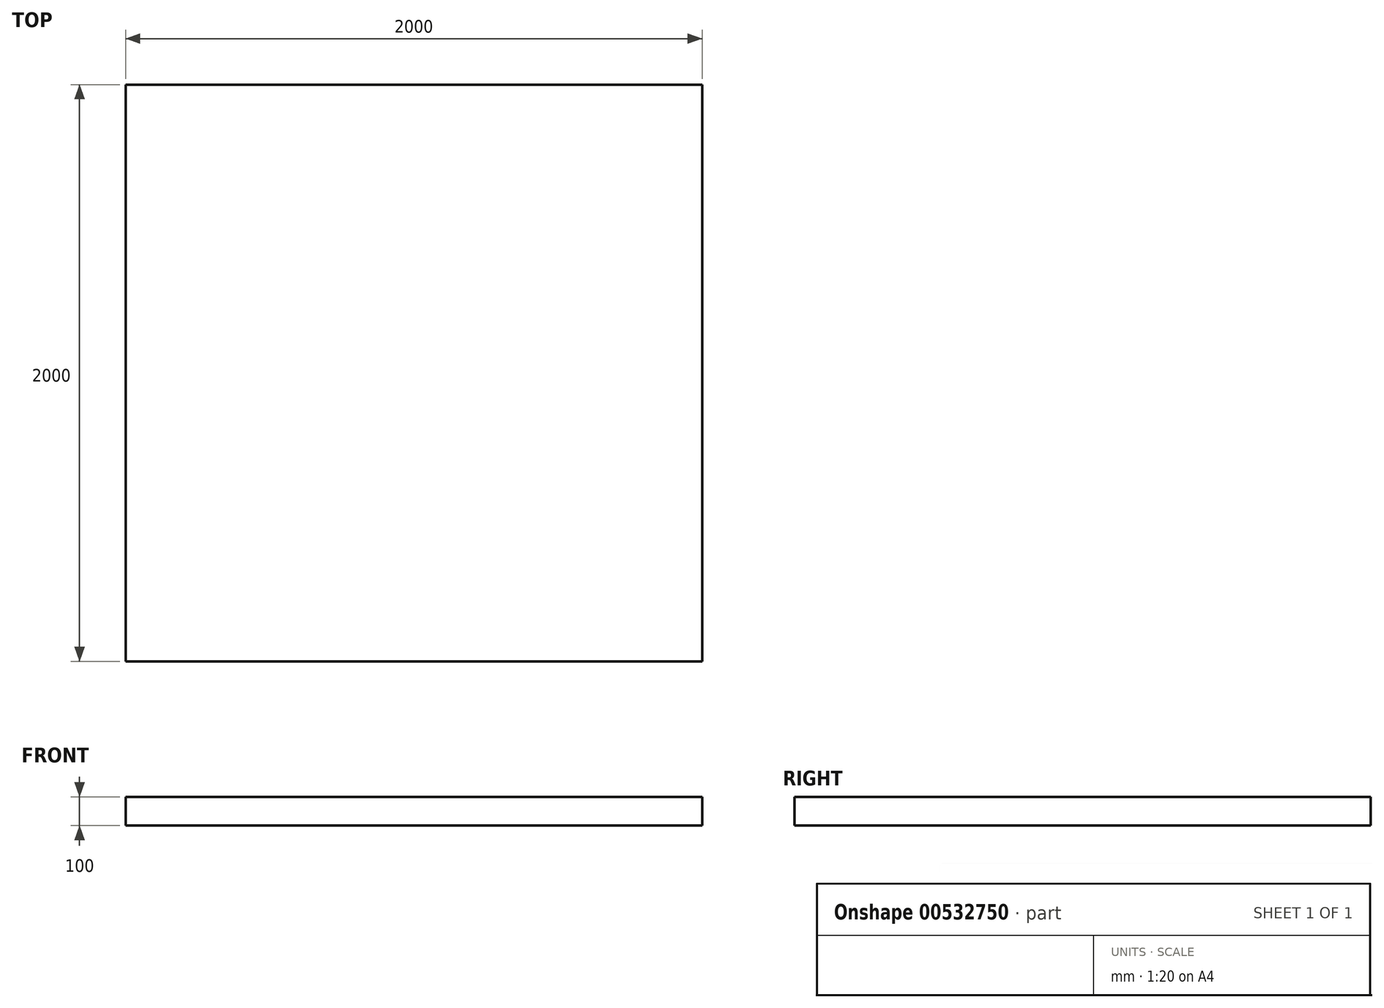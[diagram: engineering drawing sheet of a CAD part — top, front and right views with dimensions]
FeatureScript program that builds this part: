
annotation { "Feature Type Name" : "Feature", "Feature Type Description" : "" }
export const myFeature = defineFeature(function(context is Context, id is Id, definition is map)
    precondition{}
    {
        {
            var Q0;
            Q0=qCreatedBy(makeId("Top.planeOp"),FACE);
            var sketch = newSketch(context, id + "F0", { "sketchPlane" : qUnion([Q0])});
            skLineSegment(sketch, "E0.bottom", {"start": v(1000, -1000) * mm, "end": v(-1000, -1000) * mm});
            skLineSegment(sketch, "E0.top", {"start": v(1000, 1000) * mm, "end": v(-1000, 1000) * mm});
            skLineSegment(sketch, "E0.left", {"start": v(1000, -1000) * mm, "end": v(1000, 1000) * mm});
            skLineSegment(sketch, "E0.right", {"start": v(-1000, -1000) * mm, "end": v(-1000, 1000) * mm});
            skPoint(sketch, "E0.middle", {"position": v(0, 0) * mm});
            skSolve(sketch);
        }
        {
            var Q0;
            Q0=makeQuery(id+"F0.imprint","IMPRINT",FACE,{"disambiguationData":[TD([[makeQuery(id+"F0.imprint","IMPRINT",EDGE,{"derivedFrom":sQuery(id+"F0.wireOp",EDGE,"E0.bottom")}),-1.0]])]});
            extrude(context, id + "F1", {"entities" : qUnion([Q0]), "oppositeDirection" : true, "depth" : 100 * mm, "offsetDistance" : 25 * mm});
        }
    });
